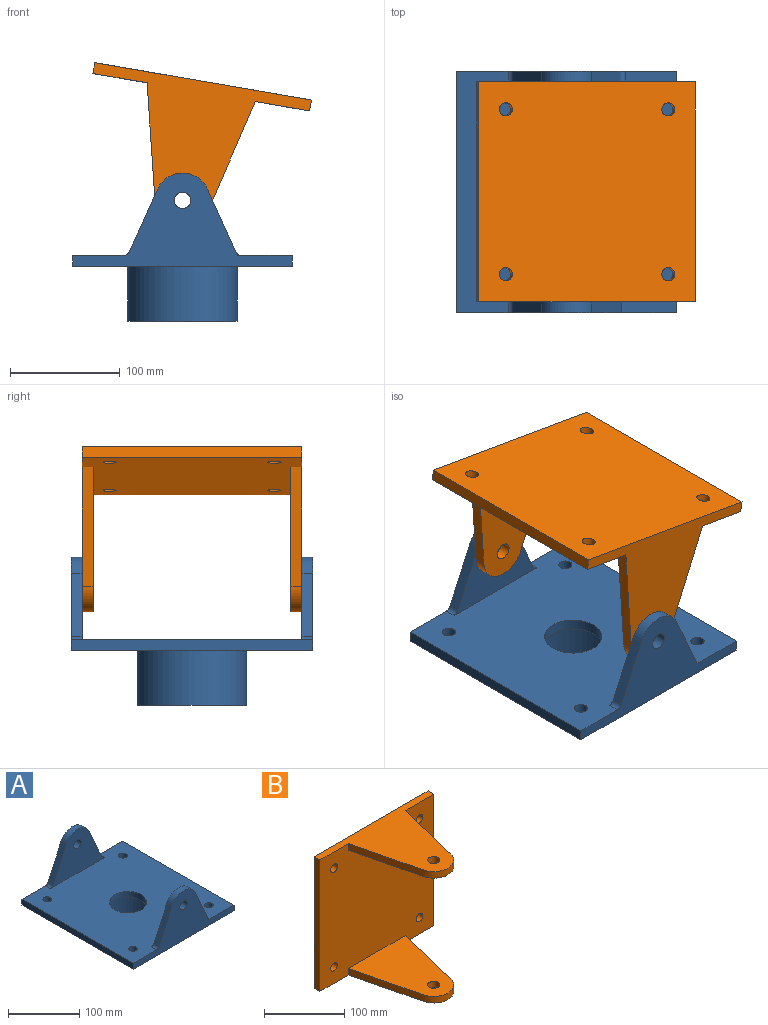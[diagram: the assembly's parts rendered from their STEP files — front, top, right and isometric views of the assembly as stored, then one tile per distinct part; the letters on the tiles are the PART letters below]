
ASSEMBLY  parts=2 mates=1
PART A: 28 faces, bbox 200x220x135 mm
  f0: plane 220x10mm, normal (-1,0,0), area 2200mm2, adj f1,f3,f4,f5
  f1: plane 200x85mm, normal (0,-1,0), area 6695.4mm2, adj f0,f2,f4,f5,f15,f16,f17,f24
  f2: plane 220x10mm, normal (1,0,0), area 2200mm2, adj f1,f3,f4,f5
  f3: plane 200x85mm, normal (0,1,0), area 6697.2mm2, adj f0,f2,f4,f5,f19,f20,f21,f23
  f4: plane 220x200mm, normal (0,0,1), area 39327mm2, adj f0,f1,f2,f3,f6,f7,f8,f9
  f5: plane 220x200mm, normal (0,0,-1), area 35693.6mm2, adj f0,f1,f2,f3,f6,f7,f8,f9
  f6: cylinder r=6mm len=12mm, axis (0,0,-1), area 377mm2, adj f4,f5
  f7: cylinder r=6mm len=12mm, axis (0,0,-1), area 377mm2, adj f4,f5
  f8: cylinder r=6mm len=12mm, axis (0,0,-1), area 377mm2, adj f4,f5
  f9: cylinder r=6mm len=12mm, axis (0,0,-1), area 377mm2, adj f4,f5
  f10: cylinder r=45mm len=90mm, axis (0,0,1), area 14137.2mm2, adj f12,f13
  f11: cylinder r=50mm len=100mm, axis (0,0,1), area 15708mm2, adj f5,f12
  f12: plane 100x100mm, normal (0,0,-1), area 1492.3mm2, adj f10,f11
  f13: plane 90x90mm, normal (0,0,-1), area 4238mm2, adj f10,f14
  f14: cylinder r=26mm len=52mm, axis (0,0,-1), area 1633.6mm2, adj f4,f13
  f15: plane 57.34x25.89mm, normal (-0.91,0,0.41), area 629.2mm2, adj f1,f17,f18,f27
  f16: plane 60.29x27.21mm, normal (0.91,0,0.41), area 661.4mm2, adj f1,f4,f17,f18
  f17: cylinder r=25mm len=45.57mm, axis (0,-1,0), area 573.4mm2, adj f1,f15,f16,f18
  f18: plane 103.23x75mm, normal (0,1,0), area 4695.4mm2, adj f4,f15,f16,f17,f24,f27
  f19: cylinder r=25mm len=45.57mm, axis (0,1,0), area 573.4mm2, adj f3,f20,f21,f22
  f20: plane 57.34x25.89mm, normal (0.91,0,0.41), area 629.2mm2, adj f3,f19,f22,f25
  f21: plane 57.34x25.89mm, normal (-0.91,0,0.41), area 629.2mm2, adj f3,f19,f22,f26
  f22: plane 106.46x75mm, normal (0,-1,0), area 4697.2mm2, adj f4,f19,f20,f21,f23,f25,f26
  f23: cylinder r=7.5mm len=15mm, axis (0,1,0), area 471.2mm2, adj f3,f22
  f24: cylinder r=7.5mm len=15mm, axis (0,1,0), area 471.2mm2, adj f1,f18
  f25: cylinder r=5mm len=10mm, axis (0,-1,0), area 57.3mm2, adj f3,f4,f20,f22
  f26: cylinder r=5mm len=10mm, axis (0,-1,0), area 57.3mm2, adj f3,f4,f21,f22
  f27: cylinder r=5mm len=10mm, axis (0,-1,0), area 57.3mm2, adj f1,f4,f15,f18
PART B: 20 faces, bbox 200x135x200 mm
  f0: plane 200x10mm, normal (-1,0,0), area 2000mm2, adj f1,f6,f8,f9
  f1: plane 200x135mm, normal (0,0,-1), area 10380.5mm2, adj f0,f2,f8,f9,f10,f11,f12,f13
  f2: plane 200x10mm, normal (1,0,0), area 2000mm2, adj f1,f6,f8,f9
  f3: cylinder r=6mm len=12mm, axis (0,1,0), area 377mm2, adj f8,f9
  f4: cylinder r=6mm len=12mm, axis (0,1,0), area 377mm2, adj f8,f9
  f5: cylinder r=6mm len=12mm, axis (0,1,0), area 377mm2, adj f8,f9
  f6: plane 200x135mm, normal (0,0,1), area 10380.5mm2, adj f0,f2,f8,f9,f15,f16,f17,f18
  f7: cylinder r=6mm len=12mm, axis (0,1,0), area 377mm2, adj f8,f9
  f8: plane 200x200mm, normal (0,-1,0), area 37547.6mm2, adj f0,f1,f2,f3,f4,f5,f6,f7
  f9: plane 200x200mm, normal (0,1,0), area 39547.6mm2, adj f0,f1,f2,f3,f4,f5,f6,f7
  f10: plane 105.9x25.71mm, normal (-0.97,-0.24,0), area 1089.7mm2, adj f1,f8,f12,f14
  f11: plane 105.9x25.71mm, normal (0.97,-0.24,0), area 1089.7mm2, adj f1,f8,f12,f14
  f12: cylinder r=25mm len=48.59mm, axis (0,0,-1), area 666.3mm2, adj f1,f10,f11,f14
  f13: cylinder r=7.5mm len=15mm, axis (0,0,-1), area 471.2mm2, adj f1,f14
  f14: plane 125x100mm, normal (0,0,1), area 8380.5mm2, adj f8,f10,f11,f12,f13
  f15: plane 105.9x25.71mm, normal (-0.97,-0.24,0), area 1089.7mm2, adj f6,f8,f16,f19
  f16: cylinder r=25mm len=48.59mm, axis (0,0,1), area 666.3mm2, adj f6,f15,f18,f19
  f17: cylinder r=7.5mm len=15mm, axis (0,0,1), area 471.2mm2, adj f6,f19
  f18: plane 105.9x25.71mm, normal (0.97,-0.24,0), area 1089.7mm2, adj f6,f8,f16,f19
  f19: plane 125x100mm, normal (0,0,-1), area 8380.5mm2, adj f8,f15,f16,f17,f18
PLACE A t=(25.4,-257.35,162.89)mm fixed
PLACE B rot(axis=(-0.06,-0.71,-0.71),173.1deg) t=(-24.04,-263.54,331.05)mm
MATE revolute B.f12 <-> A.f17  axis (0,1,0) through (-44.12,-335.49,222.89)mm
